# Revit family: 44922010
name_source: partatom
category: Plumbing Fixtures
revit_build: Autodesk Revit 2016 (Build: 20150714_1515(x64)
units: mm (PartAtom-declared; Revit-internal decimal feet)

## family parameters
Always vertical = Yes
Cut with Voids When Loaded = No
OmniClass Number = 23.45.55.00
OmniClass Title = Sanitary Faucets, Wastes
Part Type = Normal
Room Calculation Point = No
Round Connector Dimension = Use Diameter
Shared = No
Work Plane-Based = No

## types (1)
- 44922010 Cover part for washbasin faucet, 230/12 V
    2D/3D/BIM Files URL = http://static.hansa.com
    Advanced Features = Adjustable settings (with magnetic key);
    Aerator = HONEYCOMB®; CACHÉ® integrated aerator
    AssetType = Fixed
    Automatic Flush = off (off/12/24/48/72 h)
    Automatic Flush Period = 30 s (10/30/60/120/180/240/300/600 s)
    BIMObjectName = 44922010
    BodyMaterial = Brass
    Brand = Hansa
    Catalog Drawing URL = http://static.hansa.com
    Category = Bathroom
    Class = Touchless, fixed connection
    CloseOffRating = 0
    Color = Chrome
    ConvergoRefNr = 0087-1806-0022-FI
    Customs Code = 84818011
    DN Size = DN15
    Dimension Drawing URL = http://static.hansa.com
    DurationUnit = Year
    EAN Number = 4057304006685
    EMC Directive = 2014/30/EU
    EN Standard = EN 15091
    Electrical Connection = 230 / 12 V
    Electronic Parts = Infrared sensor; Control unit;
    FDV Document URL = http://www.hansa.com
    FaucetMainMaterial = Brass
    Features = Touchless
    Finish = Polished
    Flow Drawing URL = http://static.hansa.com
    Flow Rate At 300kPa = 0.1 L/s
    FlowCoefficient = 0
    Group = Washbasin faucets
    IfcExportAs = IfcValveType
    IfcExportType = FAUCET
    Included = Temperature control handle; Square wall rosette; Spout
    Installation Type = Wall-mounted concealed
    Installation and Maintenance = http://static.hansa.com
    Intelligent After Flow Period = 2 s ± 1 s (1/2/3/4/8 s)
    Lever Handle = Temperature control handle
    Long Marketing = Concealed electronic mixer, DN 15 (G1/2); Suitable for HANSAMATRIX installation unit
    ManufacterURL = http://www.hansa.com
    Manufacturer = Hansa
    ManufacturerName = Hansa
    Market = AUT;BEL;DEU;ESP;INT;NLD
    Material = Brass
    Max Flow Period = 120.0 s
    Max. Hot Water Supply = 70 °C
    Model = 44922010 Cover part for washbasin faucet, 230/12 V
    ModelReference = 44922010
    NBSDescription = Water supply fittings for baths
    NBSReference = 45-35-70/315
    Name = 44922010 Cover part for washbasin faucet, 230/12 V
    Name_en = 44922010 Cover part for washbasin faucet, 230/12 V
    NominalDepth = 213 mm  [stored 0.698819 ft]
    NominalHeight = 175 mm  [stored 0.574147 ft]
    NominalWidth = 75 mm
    Operating Voltage = 12 V
    Package Weight = 1.2 kg
    Package external Dimensions = 210 x 165 x 60
    Pressure Loss With Flow 01ls = 250000.0 Pa
    Product Code = 44922010
    Product Datasheet = http://www.hansa.com
    Product Family = HANSADESIGNO Style
    Product Image URL = http://static.hansa.com
    Product URL = http://static.hansa.com
    Projection = 195 mm  [stored 0.639764 ft]
    Protection Class = IP 55 / Transformer IP 40
    Recognition Range = ~15 cm (~10/15/17/20 cm)
    Revision = 2
    Shape = Sculptured
    Short Marketing = Trim kit
    Size = 75x213x150 mm
    Spare Parts = http://static.hansa.com
    Spout Type = Fixed spout
    Technology Sales Arguments = The right product for the modular and design-oriented concealed installation system HANSAMATRIX.
    Temperature = Thermostatic temperature control
    Uniclass2 = Pr_40_20_97_07
    Uniclass2015Description = Bath manual water supply sets
    Uniclass2015Reference = Pr_40_20_87_07
    Version = 2
    VersionDate = 01/01/2019
    WarrantyDescription = http://warranty.hansa.com
    WarrantyDurationUnit = Year
    WorkingPressure = 100 - 1000 kPa

note: [stored X ft] marks values corroborated as IEEE doubles in the binary element streams (Revit-internal decimal feet)

## geometry (parser evidence)
native form markers: Sweep x5
no freeform markers — native parametric forms only
